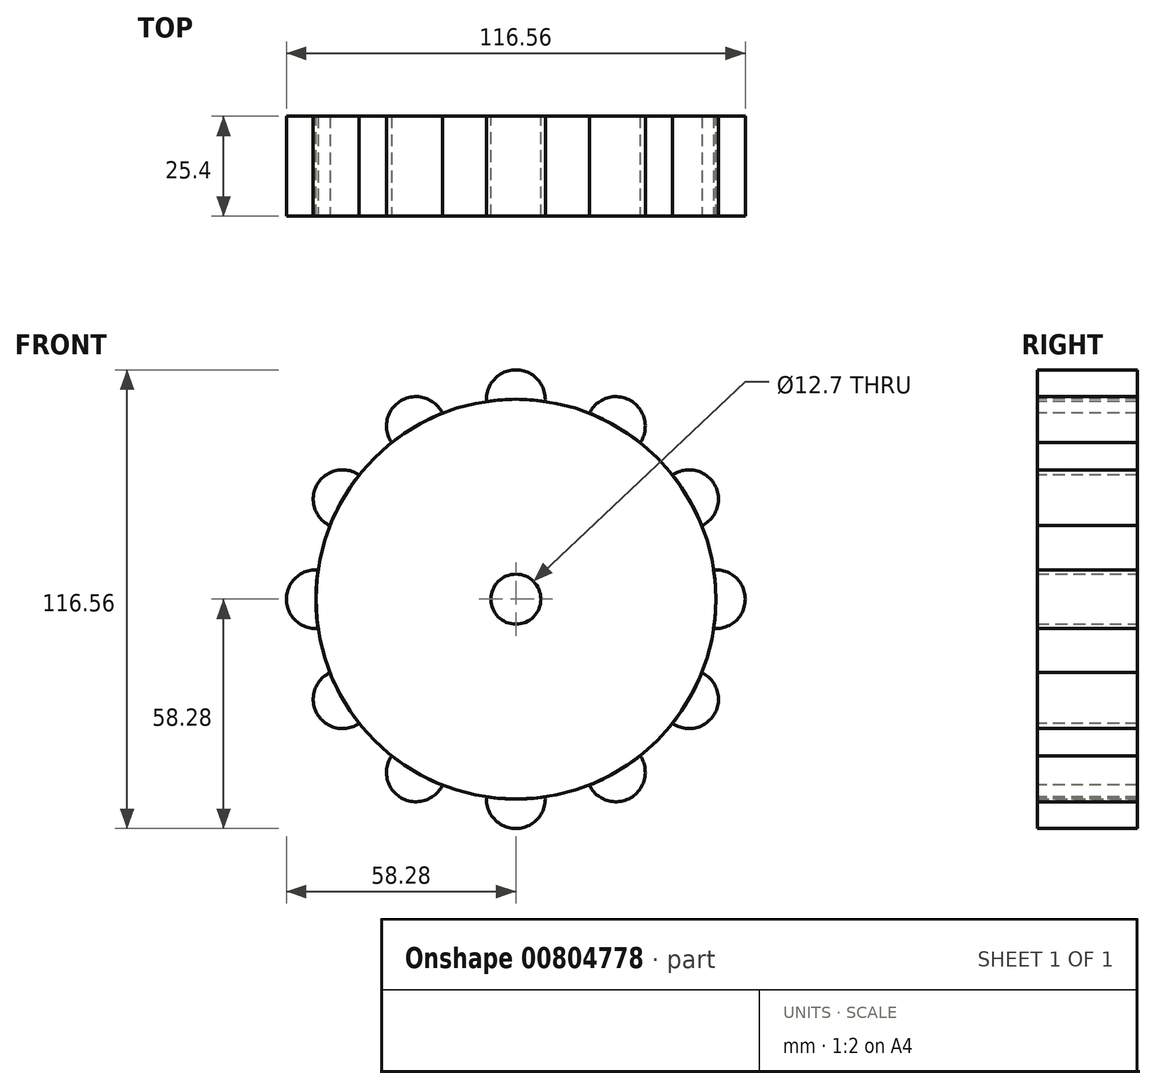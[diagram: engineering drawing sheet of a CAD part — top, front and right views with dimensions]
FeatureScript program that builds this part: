
annotation { "Feature Type Name" : "Feature", "Feature Type Description" : "" }
export const myFeature = defineFeature(function(context is Context, id is Id, definition is map)
    precondition{}
    {
        {
            var Q0;
            Q0=qCreatedBy(makeId("Front.planeOp"),FACE);
            var sketch = newSketch(context, id + "F0", { "sketchPlane" : qUnion([Q0])});
            skCircle(sketch, "E0", {"center": v(0, 0) * mm, "radius": 50.8 * mm});
            skCircle(sketch, "E1", {"center": v(0, 0) * mm, "radius": 6.35 * mm});
            skSolve(sketch);
        }
        {
            var Q0;
            Q0=makeQuery(id+"F0.imprint","IMPRINT",FACE,{"disambiguationData":[TD([[makeQuery(id+"F0.imprint","IMPRINT",EDGE,{"derivedFrom":sQuery(id+"F0.wireOp",EDGE,"E0")}),1.0]])]});
            extrude(context, id + "F1", {"entities" : qUnion([Q0]), "endBound" : BoundingType.SYMMETRIC, "depth" : 25.4 * mm, "offsetDistance" : 25.4 * mm});
        }
        {
            var Q0;
            Q0=makeQuery(id+"F1.opExtrude","CAP_FACE",FACE,{"disambiguationData":[OSD([sQuery(id+"F0.wireOp",EDGE,"E0"),sQuery(id+"F0.wireOp",EDGE,"E1")])],"isStart":false});
            var sketch = newSketch(context, id + "F2", { "sketchPlane" : qUnion([Q0])});
            skCircle(sketch, "E2", {"center": v(0, 50.8) * mm, "radius": 7.48 * mm});
            skSolve(sketch);
        }
        {
            var Q0;
            {var subQ0=sQuery(id+"F2.wireOp",EDGE,"E2");var subQ1=makeQuery(id+"F1.opExtrude","CAP_EDGE",EDGE,{"disambiguationData":[OSD([sQuery(id+"F0.wireOp",EDGE,"E0")])],"isStart":false});var subQ2=makeQuery(id+"F2.imprint","INTERSECT",VERTEX,{"disambiguationData":[OD(0.0)],"derivedFrom":[subQ1,subQ0]});Q0=makeQuery(id+"F2.imprint","IMPRINT",FACE,{"disambiguationData":[TD([[makeQuery(id+"F2.imprint","IMPRINT",EDGE,{"disambiguationData":[TD([[subQ2,1.0]])],"derivedFrom":subQ0}),1.0]])]});}
            extrude(context, id + "F3", {"entities" : qUnion([Q0]), "oppositeDirection" : true, "depth" : 25.4 * mm, "offsetDistance" : 25.4 * mm});
        }
        {
            var Q0;
            Q0=makeQuery(id+"F3.opExtrude","SWEPT_BODY",BODY,{"disambiguationData":[OSD([sQuery(id+"F0.wireOp",EDGE,"E0"),sQuery(id+"F2.wireOp",EDGE,"E2")])]});
            var Q1;
            Q1=makeQuery(id+"F1.opExtrude","CAP_EDGE",EDGE,{"disambiguationData":[OSD([sQuery(id+"F0.wireOp",EDGE,"E0")])],"isStart":false});
            circularPattern(context, id + "F4", {"entities" : qUnion([Q0]), "axis" : qUnion([Q1]), "angle" : 360 * degree, "instanceCount" : 12, "equalSpace" : true});
        }
    });
